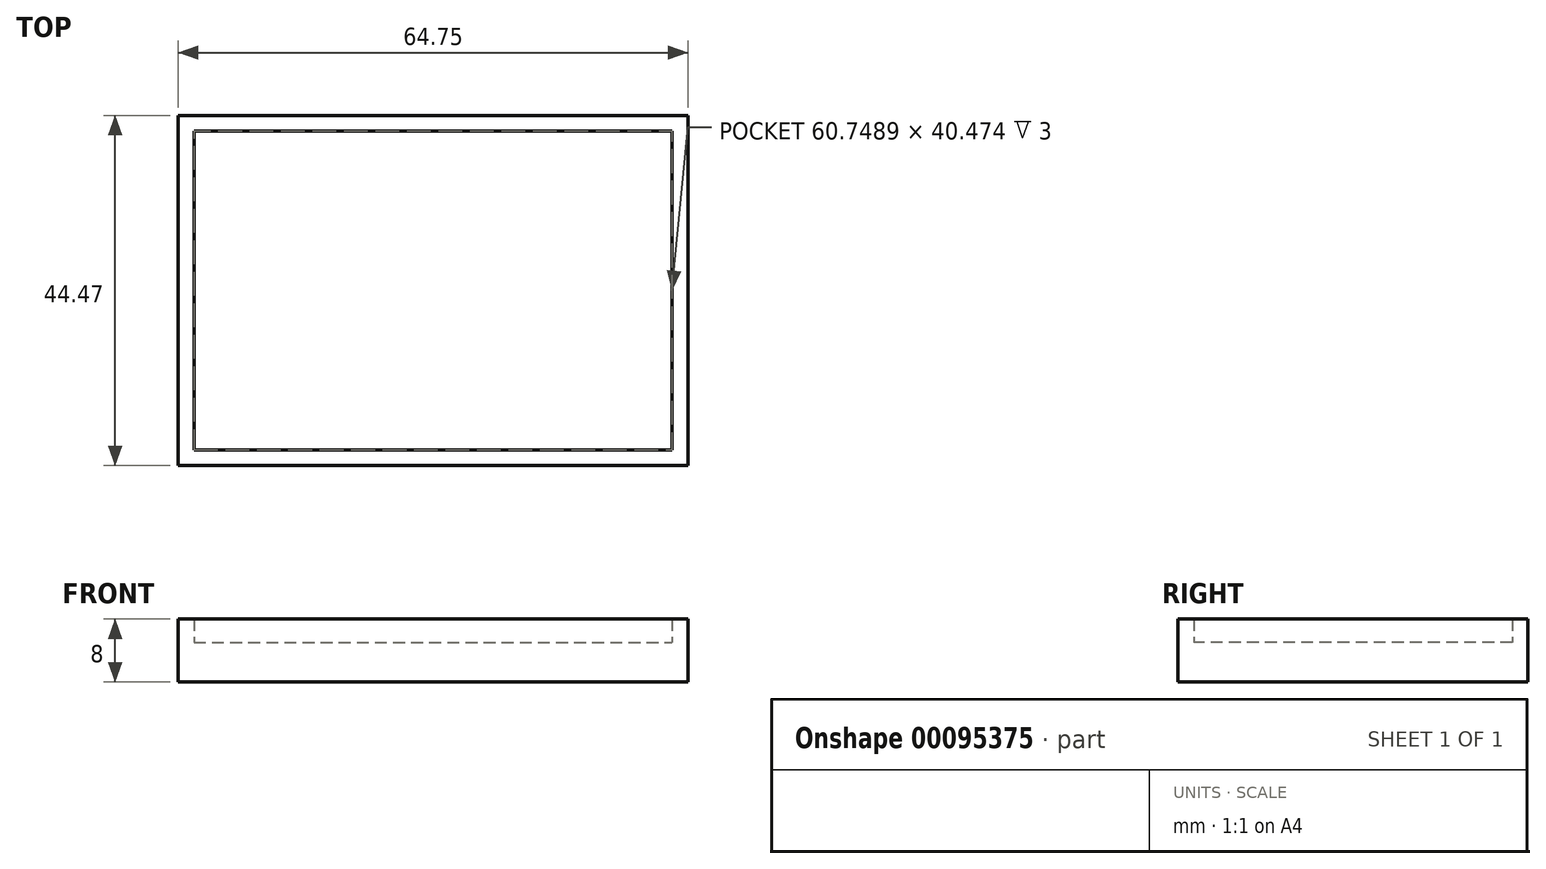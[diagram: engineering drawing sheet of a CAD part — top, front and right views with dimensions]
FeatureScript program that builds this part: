
annotation { "Feature Type Name" : "Feature", "Feature Type Description" : "" }
export const myFeature = defineFeature(function(context is Context, id is Id, definition is map)
    precondition{}
    {
        {
            var Q0;
            Q0=qCreatedBy(makeId("Top.planeOp"),FACE);
            var sketch = newSketch(context, id + "F0", { "sketchPlane" : qUnion([Q0])});
            skLineSegment(sketch, "E0.bottom", {"start": v(-35.48, 12.75) * mm, "end": v(29.27, 12.75) * mm});
            skLineSegment(sketch, "E0.top", {"start": v(-35.48, -31.72) * mm, "end": v(29.27, -31.72) * mm});
            skLineSegment(sketch, "E0.left", {"start": v(-35.48, 12.75) * mm, "end": v(-35.48, -31.72) * mm});
            skLineSegment(sketch, "E0.right", {"start": v(29.27, 12.75) * mm, "end": v(29.27, -31.72) * mm});
            skSolve(sketch);
        }
        {
            var Q0;
            Q0 = qSketchRegion(id + "F0", true);
            extrude(context, id + "F1", {"entities" : qUnion([Q0]), "depth" : 5 * mm});
        }
        {
            var Q0;
            Q0=makeQuery(id+"F1.opExtrude","CAP_FACE",FACE,{"disambiguationData":[OSD([sQuery(id+"F0.wireOp",EDGE,"E0.bottom"),sQuery(id+"F0.wireOp",EDGE,"E0.top"),sQuery(id+"F0.wireOp",EDGE,"E0.left"),sQuery(id+"F0.wireOp",EDGE,"E0.right")])],"isStart":false});
            var sketch = newSketch(context, id + "F2", { "sketchPlane" : qUnion([Q0])});
            skLineSegment(sketch, "E1.0", {"start": v(-33.48, 10.75) * mm, "end": v(-33.48, -29.72) * mm});
            skLineSegment(sketch, "E1.1", {"start": v(-33.48, 10.75) * mm, "end": v(27.27, 10.75) * mm});
            skLineSegment(sketch, "E1.2", {"start": v(27.27, 10.75) * mm, "end": v(27.27, -29.72) * mm});
            skLineSegment(sketch, "E1.3", {"start": v(-33.48, -29.72) * mm, "end": v(27.27, -29.72) * mm});
            skSolve(sketch);
        }
        {
            var Q0;
            Q0=makeQuery(id+"F2.imprint","IMPRINT",FACE,{"disambiguationData":[TD([[makeQuery(id+"F2.imprint","IMPRINT",EDGE,{"derivedFrom":sQuery(id+"F2.wireOp",EDGE,"E1.0")}),-1.0]])]});
            extrude(context, id + "F3", {"entities" : qUnion([Q0]), "operationType" : NewBodyOperationType.ADD, "depth" : 3 * mm});
        }
    });
